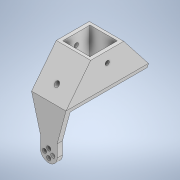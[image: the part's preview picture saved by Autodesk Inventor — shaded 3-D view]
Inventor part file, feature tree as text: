
AUTODESK INVENTOR PART (.ipt)
format: ipt  version: 2022 (Build 260153000, 153)  size: 188,928 bytes
history: native  units: mm
features: extrude x8, sketch x8, plane x1
ambient origin geometry x8: Origin, YZ Plane, XZ Plane, XY Plane, X Axis, Y Axis, Z Axis, Center Point
bodies: Solid1 (feature_tree)
feature tree (17):
  extrude  "Extrusion1"  Depth=4.0mm TaperAngle=360.0deg
  extrude  "Extrusion2"  Depth=5.0mm
  extrude  "Extrusion4"  Depth=73.5mm TaperAngle=0.0deg
  extrude  "Extrusion5"  Depth=12.7mm
  extrude  "Extrusion6"  Depth=3.0mm
  extrude  "Extrusion7"  Depth=3.0mm TaperAngle=0.0deg
  plane  "Work Plane1"
  extrude  "Extrusion8"  Depth=26.0mm
  extrude  "Extrusion9"  Depth=25.4mm TaperAngle=0.0deg
  sketch  "Sketch1"  dims[d2=4.0mm d3=40.0mm d5=360.0deg]
  sketch  "Sketch2"  dims[d16=5.0mm d17=0.0mm d18=13.25mm]
  sketch  "Sketch4"  dims[d19=2.0mm d20=0.0mm d26=73.5mm d27=0.0mm]
  sketch  "Sketch5"  dims[d28=30.0mm d29=0.0mm d30=12.7mm]
  sketch  "Sketch6"  dims[d31=12.7mm d32=3.0mm]
  sketch  "Sketch7"  dims[d33=3.0mm d34=30.0mm d35=0.0mm]
  sketch  "Sketch8"  dims[d37=13.0mm d38=26.0mm]
  sketch  "Sketch9"  dims[d39=26.0mm d40=25.4mm d41=0.0mm d43=4.0mm d44=0.0mm d45=0.0mm d47=4.0mm d48=10.0mm d49=0.0mm]
